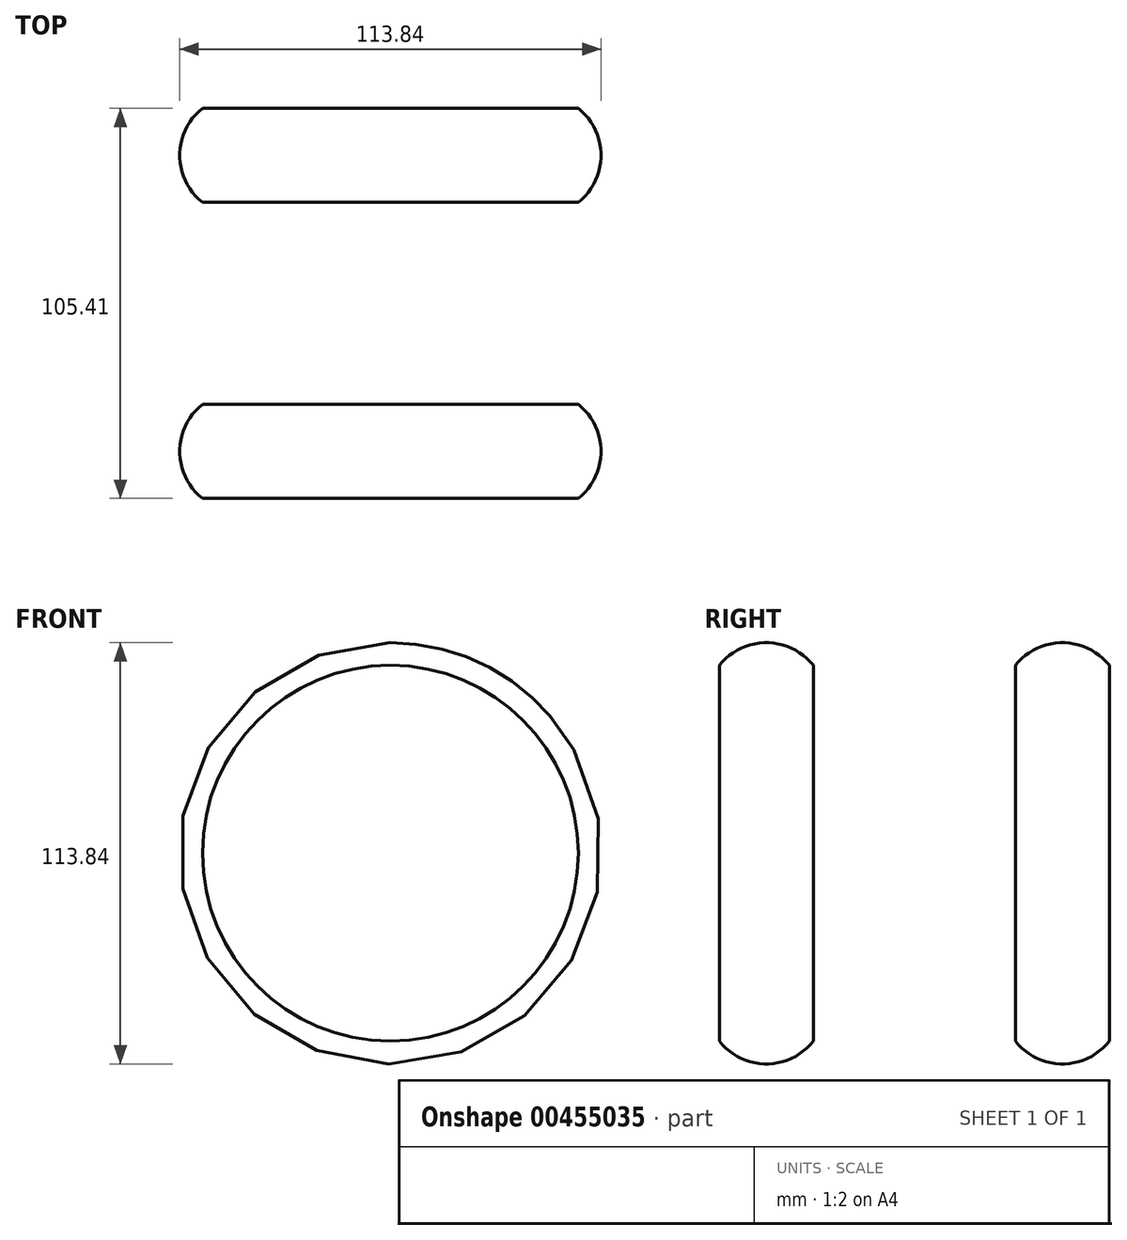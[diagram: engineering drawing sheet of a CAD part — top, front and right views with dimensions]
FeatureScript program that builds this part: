
annotation { "Feature Type Name" : "Feature", "Feature Type Description" : "" }
export const myFeature = defineFeature(function(context is Context, id is Id, definition is map)
    precondition{}
    {
        {
            var Q0;
            Q0=qCreatedBy(makeId("Top.planeOp"),FACE);
            var sketch = newSketch(context, id + "F0", { "sketchPlane" : qUnion([Q0])});
            skLineSegment(sketch, "E0.bottom", {"start": v(0, 0) * mm, "end": v(50.8, 0) * mm});
            skLineSegment(sketch, "E0.top", {"start": v(0, -25.4) * mm, "end": v(50.8, -25.4) * mm});
            skLineSegment(sketch, "E0.left", {"start": v(0, 0) * mm, "end": v(0, -25.4) * mm});
            skLineSegment(sketch, "E0.right", {"start": v(50.8, 0) * mm, "end": v(50.8, -25.4) * mm});
            skArc(sketch, "E1", {"start": v(0, 0) * mm, "mid": v(-6.12, -12.7) * mm, "end": v(0, -25.4) * mm});
            skSolve(sketch);
        }
        {
            var Q0;
            Q0 = qSketchRegion(id + "F0", true);
            var Q1;
            Q1=sQuery(id+"F0.wireOp",EDGE,"E0.right");
            revolve(context, id + "F1", {"entities" : qUnion([Q0]), "axis" : qUnion([Q1]), "revolveType" : RevolveType.FULL});
        }
        {
            var Q0;
            Q0=makeQuery(id+"F1.opRevolve","SWEPT_BODY",BODY,{"disambiguationData":[OSD([sQuery(id+"F0.wireOp",EDGE,"E0.bottom"),sQuery(id+"F0.wireOp",EDGE,"E0.top"),sQuery(id+"F0.wireOp",EDGE,"E0.right"),sQuery(id+"F0.wireOp",EDGE,"E1")])]});
            transform(context, id + "F2", {"entities" : qUnion([Q0]), "transformType" : TransformType.TRANSLATION_3D, "dx" : 0 * mm, "dy" : 80 * mm, "dz" : 0 * mm, "makeCopy" : true});
        }
    });
